# Revit family: 3420B9xx0--Sanitary_Toilets_Roca_3420B9xx0-BEYOND-Back-to-wall-vitreous-c
name_source: partatom
category: Plumbing Fixtures
units: mm (PartAtom-declared; Revit-internal decimal feet)

## family parameters
Always vertical = No
Cut with Voids When Loaded = No
OmniClass Number = 23.31.19.00
Part Type = Normal
Room Calculation Point = No
Round Connector Dimension = Use Diameter
Shared = No
Work Plane-Based = No

## types (6) — shared parameters
Always visible = Yes
BIMobject category = Toilets
BIMobject category code = sanitary-toilets
BIMobject main category = Sanitary
BIMobject main category code = sanitary
Brand url = http://www.roca.com
Date of publishing = 1/1/2022
Design country = Spain
Edition number = 1
IFC Classification = Sanitary Terminal
Manufacturer country = Spain
Manufacturer name = Roca
Material 2 = ROCA - BEYOND - Chrome
Material main = Vitreous china
Nominal height = 790 mm
Nominal width = 705 mm
OmniClass Code = 23-31 19 00
OmniClass Description = Toilets
Product Guid = 74e2c097-7b2b-4fcc-8f1e-56eba36a14e7
Product SKU = 3420B9xx0
Product data url = https://bimobject.com
Product family = Beyond
Product group = WC
Product url = http://www.roca.com
QR code = https://www.roca.com
Technical description = http://www.roca.com
Weight Net (Kg) = 0
Youtube clip = https://www.youtube.com

## per-type parameters (varying)
| type | Material 1 |
| 64 - Onyx | ROCA - BEYOND - 64 Onyx |
| 63 - Pearl | ROCA - BEYOND - 63 Pearl |
| 66 - Coffee | ROCA - BEYOND - 66 Coffee |
| 65 - Beige | ROCA - BEYOND - 65 Beige |
| 62 - Matt White | ROCA - BEYOND - 62 Matt White |
| 00 - White | ROCA - BEYOND - 00 White |

## geometry (parser evidence)
native form markers: Blend x4, Sweep x1
no freeform markers — native parametric forms only
